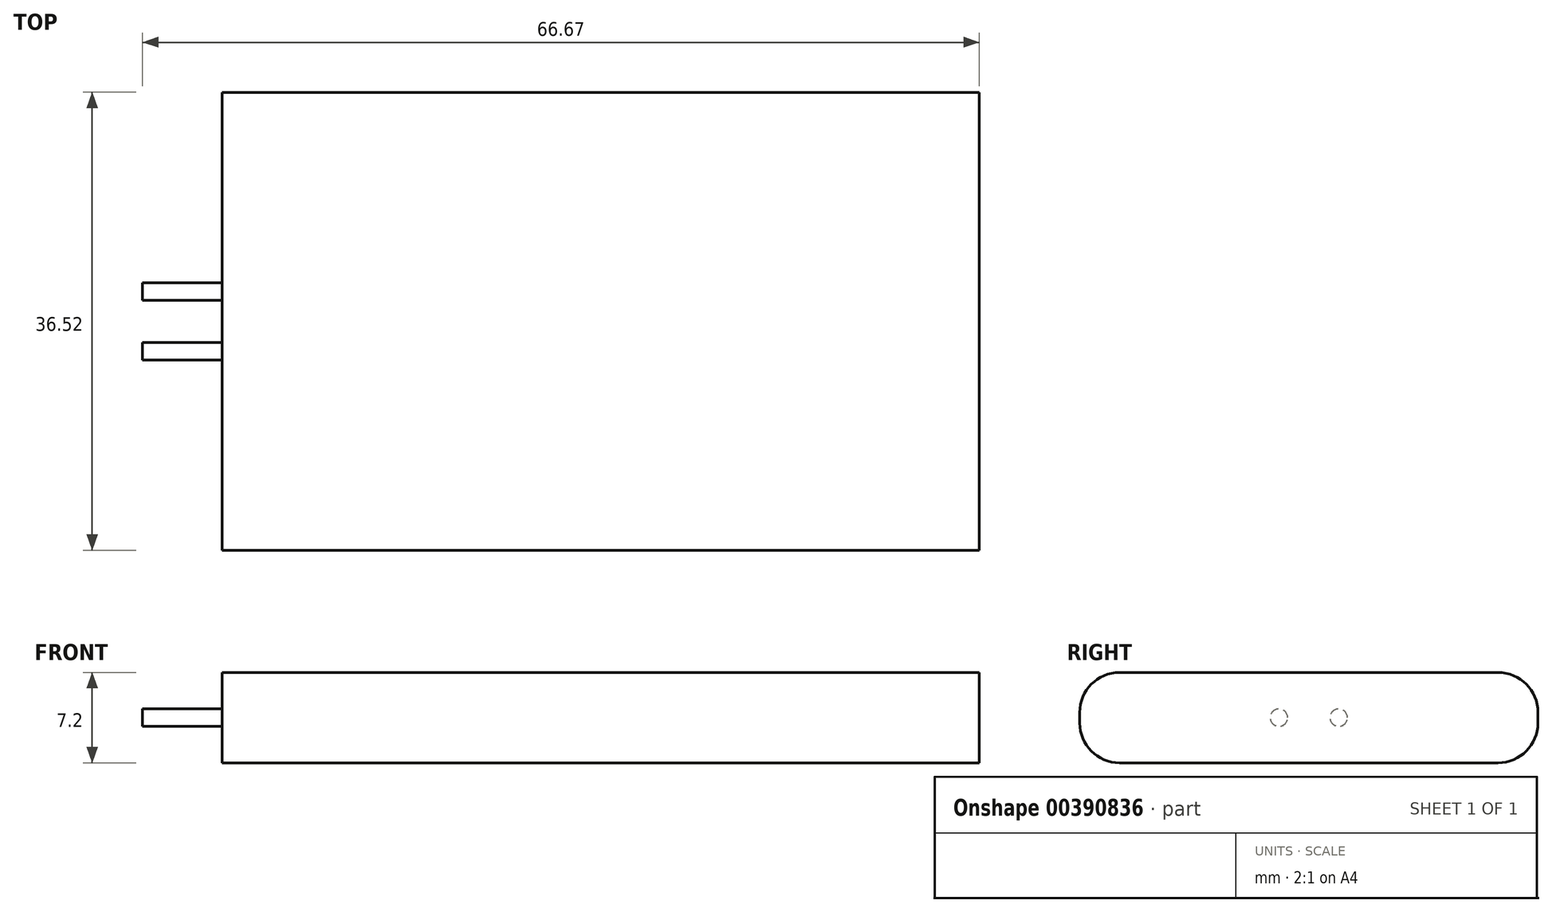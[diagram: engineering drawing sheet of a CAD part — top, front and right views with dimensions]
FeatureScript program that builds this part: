
annotation { "Feature Type Name" : "Feature", "Feature Type Description" : "" }
export const myFeature = defineFeature(function(context is Context, id is Id, definition is map)
    precondition{}
    {
        {
            var Q0;
            Q0=qCreatedBy(makeId("Top.planeOp"),FACE);
            var sketch = newSketch(context, id + "F0", { "sketchPlane" : qUnion([Q0])});
            skLineSegment(sketch, "E0.bottom", {"start": v(-30.16, 18.26) * mm, "end": v(30.16, 18.26) * mm});
            skLineSegment(sketch, "E0.top", {"start": v(-30.16, -18.26) * mm, "end": v(30.16, -18.26) * mm});
            skLineSegment(sketch, "E0.left", {"start": v(-30.16, 18.26) * mm, "end": v(-30.16, -18.26) * mm});
            skLineSegment(sketch, "E0.right", {"start": v(30.16, 18.26) * mm, "end": v(30.16, -18.26) * mm});
            skPoint(sketch, "E0.middle", {"position": v(0, 0) * mm});
            skSolve(sketch);
        }
        {
            var Q0;
            Q0 = qSketchRegion(id + "F0", true);
            extrude(context, id + "F1", {"entities" : qUnion([Q0]), "depth" : 7.2 * mm});
        }
        {
            var Q0;
            Q0=makeQuery(id+"F1.opExtrude","CAP_EDGE",EDGE,{"disambiguationData":[OSD([sQuery(id+"F0.wireOp",EDGE,"E0.top")])],"isStart":false});
            var Q1;
            Q1=makeQuery(id+"F1.opExtrude","CAP_EDGE",EDGE,{"disambiguationData":[OSD([sQuery(id+"F0.wireOp",EDGE,"E0.top")])],"isStart":true});
            var Q2;
            Q2=makeQuery(id+"F1.opExtrude","CAP_EDGE",EDGE,{"disambiguationData":[OSD([sQuery(id+"F0.wireOp",EDGE,"E0.bottom")])],"isStart":false});
            var Q3;
            Q3=makeQuery(id+"F1.opExtrude","CAP_EDGE",EDGE,{"disambiguationData":[OSD([sQuery(id+"F0.wireOp",EDGE,"E0.bottom")])],"isStart":true});
            fillet(context, id + "F2", {"entities" : qUnion([Q0, Q1, Q2, Q3]), "radius" : 3.17 * mm, "tangentPropagation" : true, "allowEdgeOverflow" : false});
        }
        {
            var Q0;
            Q0=makeQuery(id+"F1.opExtrude","SWEPT_FACE",FACE,{"disambiguationData":[OSD([sQuery(id+"F0.wireOp",EDGE,"E0.left")])]});
            var sketch = newSketch(context, id + "F3", { "sketchPlane" : qUnion([Q0])});
            skCircle(sketch, "E1", {"center": v(-2.38, 3.6) * mm, "radius": 0.7 * mm});
            skSolve(sketch);
        }
        {
            var Q0;
            Q0 = qSketchRegion(id + "F3", true);
            extrude(context, id + "F4", {"entities" : qUnion([Q0]), "depth" : 6.35 * mm});
        }
        {
            var Q0;
            Q0=makeQuery(id+"F4.opExtrude","SWEPT_BODY",BODY,{"disambiguationData":[OSD([sQuery(id+"F3.wireOp",EDGE,"E1")])]});
            var Q1;
            Q1=qCreatedBy(makeId("Front.planeOp"),FACE);
            mirror(context, id + "F5", {"entities" : qUnion([Q0]), "mirrorPlane" : qUnion([Q1])});
        }
    });
